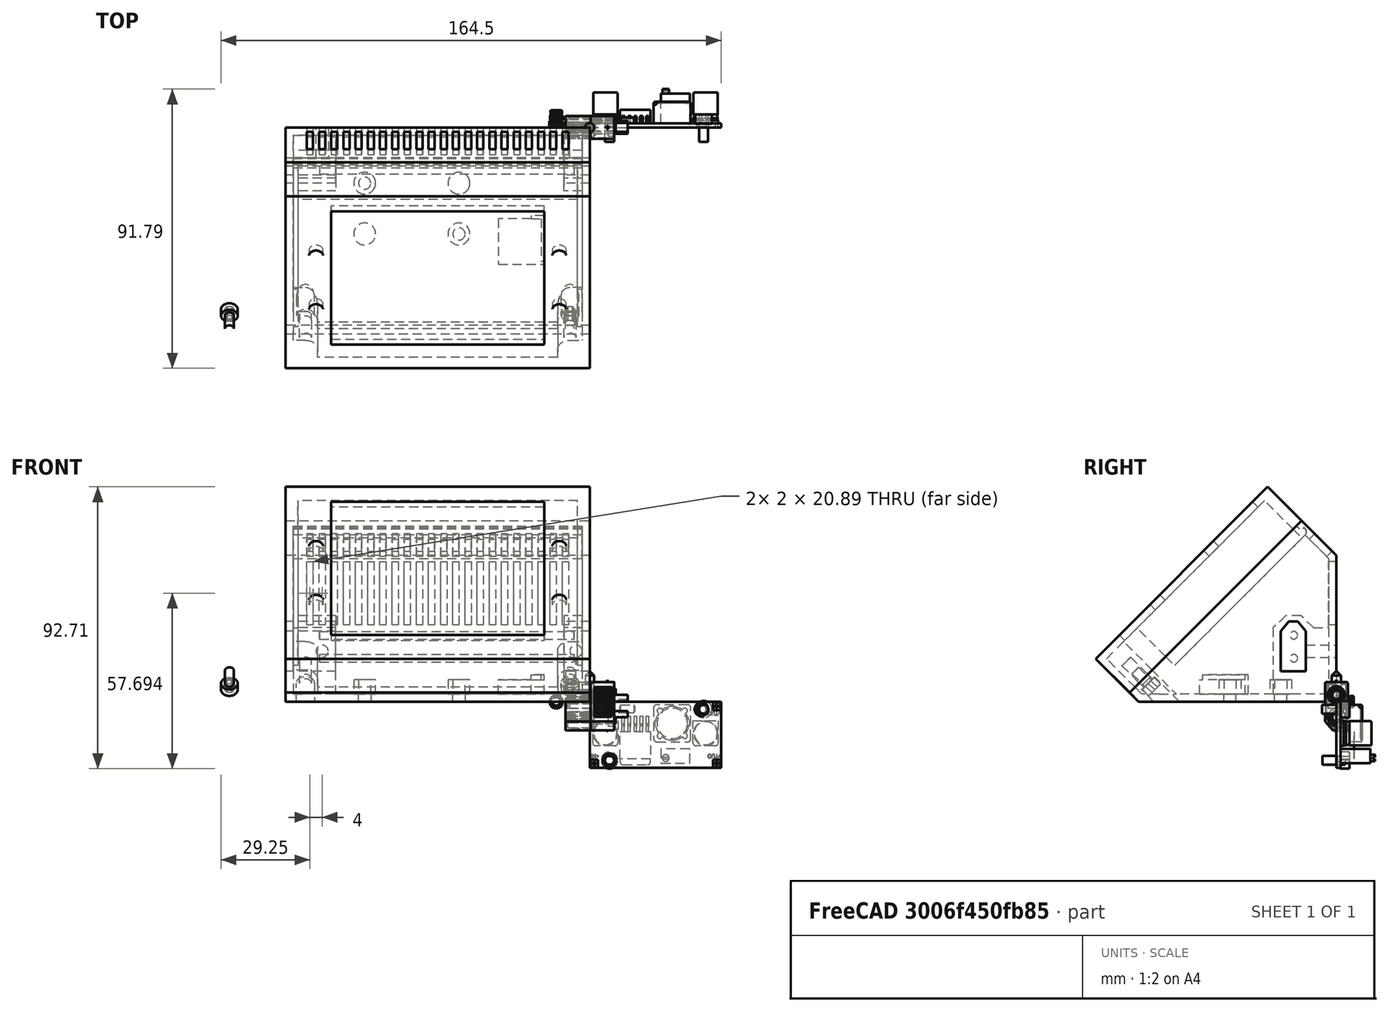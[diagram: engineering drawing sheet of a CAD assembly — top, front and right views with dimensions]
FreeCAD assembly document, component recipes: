
FREECAD ASSEMBLY — COMPONENT RECIPES ("ventilo_014surBase35mm_008.1")

This assembly document has 15 components, labeled P0..P14 below (a component is one placed body or linked part). 9 of them carry a construction recipe — the FreeCAD feature program that regenerates the part from scratch, quoted from this document or its linked companion documents; the rest are supplied as boundary geometry only. No exploded tour is included for this assembly.
COMPONENT P0 — recipe-attached ("base", modeled in this document).
Construction recipe (the document's own serialized feature program — sketch geometry with constraints, then the solid features built on it; lengths are millimeters unless a unit is written):

FEATURE [PartDesign::FeatureBase] Clone
  BaseFeature = -> Slice_child0
FEATURE [PartDesign::Thickness] Thickness
  Base = -> Clone [Face7]
  BaseFeature = -> Clone
  Intersection = false
  Join = 0
  Mode = 0
  Reversed = true
  SupportTransform = false
  Value = 2.5
  expr: Value = <<sp>>.epaisseurParois
FEATURE [PartDesign::Plane] DatumPlane001  label="planXt"
  AttachmentOffset = pos=(0,0,-2.5) rot=(0,0,1;0rad)
  Length = 110.737
  MapMode = 5
  Placement = pos=(-2.5,6e-16,-6e-16) rot=(0.57735,0.57735,0.57735;2.0944rad)
  ResizeMode = 0
  Support = -> [YZ_Plane002]
  Width = 102.305
  expr: .AttachmentOffset.Base.z = -<<sp>>.epaisseurParois
FEATURE [Sketcher::SketchObject] Sketch002  label="sk_renfortXt"
  FullyConstrained = true
  MapMode = 5
  Placement = pos=(-2.5,6e-16,-6e-16) rot=(0.57735,0.57735,0.57735;2.0944rad)
  Support = -> [DatumPlane001]
  expr: .Constraints.dist = <<sp>>.xt60distanceAngleBord
  expr: .Constraints.epRf = <<sp>>.xt60epRenfort
  expr: Constraints[13] = <<sp>>.xt60largeurFetiere
  expr: Constraints[14] = <<sp>>.xt60hauteur
  expr: Constraints[15] = <<sp>>.xt60hauteurToit
  expr: Constraints[16] = <<sp>>.xt60base
  expr: Constraints[18] = .Constraints.dist
  expr: Constraints[31] = <<sp>>.epaisseurParois
  expr: Constraints[32] = .Constraints.epRf
  expr: Constraints[34] = .Constraints.epRf
  expr: Constraints[45] = <<sp>>.epaisseurParois
  sketch-geometry (17):
    g0: LineSegment StartX=-18.3 StartY=10 StartZ=0 EndX=-18.3 EndY=23.25 EndZ=0
    g1: LineSegment StartX=-18.3 StartY=23.25 StartZ=0 EndX=-15.65 EndY=25.75 EndZ=0
    g2: LineSegment StartX=-15.65 StartY=25.75 StartZ=0 EndX=-12.65 EndY=25.75 EndZ=0
    g3: LineSegment StartX=-12.65 StartY=25.75 StartZ=0 EndX=-10 EndY=23.25 EndZ=0
    g4: LineSegment StartX=-10 StartY=23.25 StartZ=0 EndX=-10 EndY=10 EndZ=0
    g5: LineSegment StartX=-10 StartY=10 StartZ=0 EndX=-18.3 EndY=10 EndZ=0
    g6: LineSegment StartX=-14.15 StartY=10 StartZ=0 EndX=-14.15 EndY=25.75 EndZ=0
    g7: LineSegment StartX=-16.6431 StartY=28.25 StartZ=0 EndX=-20.8 EndY=24.3284 EndZ=0
    g8: LineSegment StartX=-20.8 StartY=24.3284 StartZ=0 EndX=-20.8 EndY=2.5 EndZ=0
    g9: LineSegment StartX=-20.8 StartY=2.5 StartZ=0 EndX=-7.5 EndY=2.5 EndZ=0
    g10: LineSegment StartX=-7.5 StartY=2.5 StartZ=0 EndX=-7.5 EndY=24.3284 EndZ=0
    g11: LineSegment StartX=-7.5 StartY=24.3284 StartZ=0 EndX=-11.6569 EndY=28.25 EndZ=0
    g12: LineSegment StartX=-11.6569 StartY=28.25 StartZ=0 EndX=-16.6431 EndY=28.25 EndZ=0
    g13: LineSegment StartX=-7.5 StartY=24.3284 StartZ=0 EndX=-2.5 EndY=24.3284 EndZ=0
    g14: LineSegment StartX=-2.5 StartY=24.3284 StartZ=0 EndX=-2.5 EndY=2.5 EndZ=0
    g15: LineSegment StartX=-2.5 StartY=2.5 StartZ=0 EndX=-7.5 EndY=2.5 EndZ=0
    g16: LineSegment StartX=-7.5 StartY=2.5 StartZ=0 EndX=-7.5 EndY=24.3284 EndZ=0
  constraints (46):
    c: Vertical(g0)
    c: Coincident(g0,g1)
    c: Coincident(g1,g2)
    c: Horizontal(g2)
    c: Coincident(g2,g3)
    c: Coincident(g3,g4)
    c: Vertical(g4)
    c: Coincident(g4,g5)
    c: Coincident(g5,g0)
    c: Horizontal(g5)
    c: Symmetric(g1,g2,g6)
    c: Equal(g0,g4)
    c: Symmetric(g0,g4,g6)
    c: DistanceX(g2,g2) = 3
    c: DistanceY(g4,g4) = 13.25
    c: DistanceY(g3,g2) = 2.5
    c: DistanceX(g5,g5) = 8.3
    c: DistanceX(g4,g-1) = 10  'dist'
    c: DistanceY(g-1,g4) = 10
    c: Coincident(g7,g8)
    c: Vertical(g8)
    c: Coincident(g8,g9)
    c: Horizontal(g9)
    c: Coincident(g9,g10)
    c: Coincident(g10,g11)
    c: Coincident(g11,g12)
    c: Coincident(g12,g7)
    c: Symmetric(g7,g10,g6)
    c: Symmetric(g7,g11,g6)
    c: Symmetric(g8,g9,g6)
    c: DistanceX(g8,g0) = 2.5  'epRf'
    c: DistanceY(g-1,g9) = 2.5
    c: Distance(g7,g1) = 2.5
    c: Parallel(g1,g7)
    c: DistanceY(g2,g11) = 2.5
    c: Coincident(g13,g14)
    c: Coincident(g14,g15)
    c: Coincident(g15,g16)
    c: Coincident(g16,g13)
    c: Horizontal(g13)
    c: Horizontal(g15)
    c: Vertical(g14)
    c: Vertical(g16)
    c: Coincident(g13,g11)
    c: Horizontal(g14,g9)
    c: DistanceX(g14,g-1) = 2.5
FEATURE [PartDesign::Pad] Pad001  label="renfortXt"
  AllowMultiFace = false
  BaseFeature = -> Thickness
  Direction = (1,1,1)
  Length = 95
  Length2 = 100
  Profile = -> Sketch002
  Reversed = true
  Type = 0
  expr: Length = <<sp>>.largeurModuleBase - 2 * <<sp>>.epaisseurParois
FEATURE [Sketcher::SketchObject] Sketch003  label="sk_trouXt"
  FullyConstrained = true
  MapMode = 5
  Placement = pos=(0,0,0) rot=(0.57735,0.57735,0.57735;2.0944rad)
  Support = -> [YZ_Plane002]
  expr: .Constraints.dist = <<sp>>.xt60distanceAngleBord
  expr: Constraints[13] = <<sp>>.xt60base
  expr: Constraints[14] = <<sp>>.xt60hauteur
  expr: Constraints[15] = <<sp>>.xt60hauteurToit + <<sp>>.xtJeu
  expr: Constraints[16] = <<sp>>.xt60largeurFetiere
  expr: Constraints[18] = .Constraints.dist
  sketch-geometry (7):
    g0: LineSegment StartX=-18.3 StartY=10 StartZ=0 EndX=-18.3 EndY=23.25 EndZ=0
    g1: LineSegment StartX=-18.3 StartY=23.25 StartZ=0 EndX=-15.65 EndY=26.35 EndZ=0
    g2: LineSegment StartX=-15.65 StartY=26.35 StartZ=0 EndX=-12.65 EndY=26.35 EndZ=0
    g3: LineSegment StartX=-12.65 StartY=26.35 StartZ=0 EndX=-10 EndY=23.25 EndZ=0
    g4: LineSegment StartX=-10 StartY=23.25 StartZ=0 EndX=-10 EndY=10 EndZ=0
    g5: LineSegment StartX=-10 StartY=10 StartZ=0 EndX=-18.3 EndY=10 EndZ=0
    g6: LineSegment StartX=-14.15 StartY=10 StartZ=0 EndX=-14.15 EndY=26.35 EndZ=0
  constraints (19):
    c: Vertical(g0)
    c: Coincident(g0,g1)
    c: Coincident(g1,g2)
    c: Horizontal(g2)
    c: Coincident(g2,g3)
    c: Coincident(g3,g4)
    c: Coincident(g4,g5)
    c: Coincident(g5,g0)
    c: Horizontal(g5)
    c: Symmetric(g1,g2,g6)
    c: Symmetric(g0,g3,g6)
    c: Vertical(g6)
    c: Symmetric(g0,g4,g6)
    c: DistanceX(g5,g5) = 8.3
    c: DistanceY(g4,g4) = 13.25
    c: DistanceY(g3,g2) = 3.1
    c: DistanceX(g2,g2) = 3
    c: DistanceX(g4,g-1) = 10  'dist'
    c: DistanceY(g-1,g4) = 10
FEATURE [PartDesign::Pocket] Pocket
  AllowMultiFace = false
  BaseFeature = -> Pad001
  Direction = (1,1,1)
  Length = 100
  Length2 = 100
  Profile = -> Sketch003
  Type = 0
  expr: Length = <<sp>>.largeurModuleBase
FEATURE [PartDesign::Plane] DatumPlane002  label="planDecoupeRenfortXt"
  AttachmentOffset = pos=(0,0,2.5) rot=(0,0,1;0rad)
  Length = 145.563
  MapMode = 5
  Placement = pos=(0,-2.5,-6e-16) rot=(1,0,0;1.5708rad)
  ResizeMode = 0
  Support = -> [XZ_Plane002]
  Width = 105.132
  expr: .AttachmentOffset.Base.z = <<sp>>.epaisseurParois
FEATURE [Sketcher::SketchObject] Sketch004  label="sk_decoupRenfXt"
  FullyConstrained = true
  MapMode = 5
  Placement = pos=(0,-2.5,-6e-16) rot=(1,0,0;1.5708rad)
  Support = -> [DatumPlane002]
  expr: Constraints[10] = <<sp>>.xt60LongueurRenfortPetit + <<sp>>.epaisseurParois
  expr: Constraints[11] = <<sp>>.largeurModuleBase - (<<sp>>.xt60longueurRenfortGrand + <<sp>>.epaisseurParois)
  expr: Constraints[8] = <<sp>>.epaisseurParois
  expr: Constraints[9] = <<sp>>.xt60distanceAngleBord + <<sp>>.xt60hauteur + <<sp>>.xt60hauteurToit + <<sp>>.xt60epRenfort
  sketch-geometry (4):
    g0: LineSegment StartX=-83.5 StartY=28.25 StartZ=0 EndX=-8.5 EndY=28.25 EndZ=0
    g1: LineSegment StartX=-8.5 StartY=28.25 StartZ=0 EndX=-8.5 EndY=2.5 EndZ=0
    g2: LineSegment StartX=-8.5 StartY=2.5 StartZ=0 EndX=-83.5 EndY=2.5 EndZ=0
    g3: LineSegment StartX=-83.5 StartY=2.5 StartZ=0 EndX=-83.5 EndY=28.25 EndZ=0
  constraints (12):
    c: Coincident(g0,g1)
    c: Coincident(g1,g2)
    c: Coincident(g2,g3)
    c: Coincident(g3,g0)
    c: Horizontal(g0)
    c: Horizontal(g2)
    c: Vertical(g1)
    c: Vertical(g3)
    c: DistanceY(g-1,g1) = 2.5
    c: DistanceY(g-1,g0) = 28.25
    c: DistanceX(g1,g-1) = 8.5
    c: DistanceX(g2,g-1) = 83.5
FEATURE [PartDesign::Pocket] Pocket001  label="decoupeRenfXt"
  AllowMultiFace = false
  BaseFeature = -> Pocket
  Direction = (1,1,1)
  Length = 23.3
  Length2 = 100
  Profile = -> Sketch004
  Reversed = true
  Type = 0
  expr: Length = <<sp>>.xt60distanceAngleBord + <<sp>>.xt60base + 2 * <<sp>>.xt60epRenfort
FEATURE [Sketcher::SketchObject] Sketch005  label="xt60PercagePostMale"
  FullyConstrained = true
  MapMode = 5
  Placement = pos=(0,0,0) rot=(1,0,0;1.5708rad)
  Support = -> [XZ_Plane002]
  expr: Constraints[0] = <<sp>>.insertDiamPercage
  expr: Constraints[1] = <<sp>>.insertDistanceTrouBordMale
  expr: Constraints[2] = <<sp>>.insertHauteur
  sketch-geometry (1):
    g0: Circle CenterX=-4.5 CenterY=16.625 CenterZ=0 NormalX=0 NormalY=0 NormalZ=1 AngleXU=0 Radius=2
  constraints (3):
    c: Diameter(g0) = 4
    c: DistanceX(g0,g-1) = 4.5
    c: DistanceY(g-1,g0) = 16.625
FEATURE [PartDesign::Pocket] Pocket002  label="insertXtMale"
  AllowMultiFace = false
  BaseFeature = -> Pocket001
  Direction = (1,1,1)
  Length = 10
  Length2 = 100
  Profile = -> Sketch005
  Reversed = true
  Type = 0
  expr: Length = <<sp>>.insertProfondeurPercage
FEATURE [Sketcher::SketchObject] Sketch006  label="xt60PercagePostFem"
  FullyConstrained = true
  MapMode = 5
  Placement = pos=(0,0,0) rot=(1,0,0;1.5708rad)
  Support = -> [XZ_Plane002]
  expr: Constraints[0] = <<sp>>.insertDiamPercage
  expr: Constraints[1] = <<sp>>.insertDistanceTrouBordFem
  expr: Constraints[2] = <<sp>>.insertHauteur
  sketch-geometry (1):
    g0: Circle CenterX=-88 CenterY=16.625 CenterZ=0 NormalX=0 NormalY=0 NormalZ=1 AngleXU=0 Radius=2
  constraints (3):
    c: Diameter(g0) = 4
    c: DistanceX(g0,g-1) = 88
    c: DistanceY(g-1,g0) = 16.625
FEATURE [PartDesign::Pocket] Pocket003  label="insertXt60Fem"
  AllowMultiFace = false
  BaseFeature = -> Pocket002
  Direction = (1,1,1)
  Length = 10
  Length2 = 100
  Profile = -> Sketch006
  Reversed = true
  Type = 0
  expr: Length = <<sp>>.insertProfondeurPercage
FEATURE [PartDesign::Plane] DatumPlane003
  AttachmentOffset = pos=(0,0,2.5) rot=(0,0,1;0rad)
  Length = 146.564
  MapMode = 2
  Placement = pos=(0,0,2.5) rot=(0,0,1;0rad)
  ResizeMode = 0
  Support = -> [XY_Plane002]
  Width = 114.564
  expr: .AttachmentOffset.Base.z = <<sp>>.epaisseurParois
FEATURE [PartDesign::Plane] DatumPlane004  label="planTrancheur"
  AttachmentOffset = pos=(0,0,71) rot=(-1,0,0;0.785398rad)
  Length = 150.056
  MapMode = 5
  Placement = pos=(0,-71,-1.58e-14) rot=(1,0,0;0.785398rad)
  ResizeMode = 0
  Support = -> [XZ_Plane002]
  Width = 150.616
  expr: .AttachmentOffset.Base.z = <<sp>>.planTrancheur
FEATURE [Sketcher::SketchObject] Sketch008
  FullyConstrained = true
  MapMode = 5
  Placement = pos=(0,-71,-2.13e-14) rot=(1,0,0;0.785398rad)
  Support = -> [DatumPlane004]
  expr: .Constraints.dist = <<sp>>.epaisseurParois
  expr: Constraints[13] = <<sp>>.epaisseurParois
  expr: Constraints[16] = <<sp>>.insertDiamPercage / 2 + <<sp>>.insertFAVMargeDist
  expr: Constraints[1] = <<sp>>.insertFavDistAuZeroDuPLan
  expr: Constraints[21] = <<sp>>.insertFAVDistBord
  expr: Constraints[22] = <<sp>>.largeurModuleBase - <<sp>>.epaisseurParois
  sketch-geometry (7):
    g0: LineSegment StartX=-2.5 StartY=4.24264 StartZ=0 EndX=-97.5 EndY=4.24264 EndZ=0
    g1: LineSegment StartX=-6.5 StartY=14.7426 StartZ=0 EndX=-2.5 EndY=14.7426 EndZ=0
    g2: LineSegment StartX=-2.5 StartY=14.7426 StartZ=0 EndX=-2.5 EndY=6.74264 EndZ=0
    g3: LineSegment StartX=-2.5 StartY=6.74264 StartZ=0 EndX=-10.5 EndY=6.74264 EndZ=0
    g4: LineSegment StartX=-10.5 StartY=6.74264 StartZ=0 EndX=-10.5 EndY=10.7426 EndZ=0
    g5: ArcOfCircle CenterX=-6.5 CenterY=10.7426 CenterZ=0 NormalX=0 NormalY=0 NormalZ=1 AngleXU=0 Radius=4 StartAngle=1.5708 EndAngle=3.14159
    g6: LineSegment StartX=-6.5 StartY=10.7426 StartZ=0 EndX=-6.5 EndY=6.74264 EndZ=0
  constraints (23):
    c: Horizontal(g0)
    c: DistanceY(g-1,g0) = 4.24264
    c: DistanceX(g0,g-1) = 2.5  'dist'
    c: Horizontal(g1)
    c: Coincident(g1,g2)
    c: Vertical(g2)
    c: Coincident(g2,g3)
    c: Horizontal(g3)
    c: Coincident(g3,g4)
    c: Vertical(g4)
    c: Vertical(g2,g0)
    c: Equal(g3,g2)
    c: Equal(g4,g1)
    c: DistanceY(g0,g2) = 2.5
    c: Coincident(g5,g4)
    c: Coincident(g5,g1)
    c: DistanceX(g5,g2) = 4
    c: Coincident(g6,g5)
    c: PointOnObject(g6,g3)
    c: Vertical(g6)
    c: Vertical(g5,g1)
    c: DistanceX(g3,g3) = 8
    c: DistanceX(g0,g-1) = 97.5
FEATURE [PartDesign::Pad] Pad003  label="padTrouFAVDroite"
  AllowMultiFace = false
  BaseFeature = -> Pocket003
  Direction = (1,1,1)
  Length = 10
  Length2 = 100
  Profile = -> Sketch008
  Reversed = true
  Type = 3
  UpToFace = -> DatumPlane003
FEATURE [Sketcher::SketchObject] Sketch009
  FullyConstrained = true
  MapMode = 5
  Placement = pos=(0,-71,-2.13e-14) rot=(1,0,0;0.785398rad)
  Support = -> [DatumPlane004]
  expr: .Constraints.larg = <<sp>>.insertFAVDistBord
  expr: Constraints[11] = .Constraints.larg / 2
  expr: Constraints[12] = <<sp>>.largeurModuleBase
  expr: Constraints[13] = <<sp>>.insertFavDistAuZeroDuPLan
  expr: Constraints[14] = <<sp>>.epaisseurParois
  expr: Constraints[15] = <<sp>>.epaisseurParois
  expr: Constraints[8] = .Constraints.larg
  sketch-geometry (6):
    g0: LineSegment StartX=-97.5 StartY=6.74264 StartZ=0 EndX=-89.5 EndY=6.74264 EndZ=0
    g1: LineSegment StartX=-89.5 StartY=6.74264 StartZ=0 EndX=-89.5 EndY=10.7426 EndZ=0
    g2: LineSegment StartX=-93.5 StartY=14.7426 StartZ=0 EndX=-97.5 EndY=14.7426 EndZ=0
    g3: LineSegment StartX=-97.5 StartY=14.7426 StartZ=0 EndX=-97.5 EndY=6.74264 EndZ=0
    g4: ArcOfCircle CenterX=-93.5 CenterY=10.7426 CenterZ=0 NormalX=0 NormalY=0 NormalZ=1 AngleXU=0 Radius=4 StartAngle=1e-16 EndAngle=1.5708
    g5: GeomPoint X=-100 Y=4.24264 Z=0
  constraints (16):
    c: Coincident(g0,g1)
    c: Coincident(g2,g3)
    c: Coincident(g3,g0)
    c: Horizontal(g0)
    c: Horizontal(g2)
    c: Vertical(g1)
    c: Vertical(g3)
    c: DistanceX(g0,g0) = 8  'larg'
    c: DistanceY(g3,g3) = 8
    c: Tangent(g2,g4) = -1.5708
    c: Tangent(g1,g4) = -1.5708
    c: DistanceX(g0,g4) = 4
    c: DistanceX(g5,g-1) = 100
    c: DistanceY(g-1,g5) = 4.24264
    c: DistanceX(g5,g0) = 2.5
    c: DistanceY(g5,g0) = 2.5
FEATURE [PartDesign::Pad] Pad004  label="padTrouFavGauche"
  AllowMultiFace = false
  BaseFeature = -> Pad003
  Direction = (1,1,1)
  Length = 10
  Length2 = 100
  Profile = -> Sketch009
  Type = 3
  UpToFace = -> DatumPlane003 [Plane]
FEATURE [Sketcher::SketchObject] Sketch010
  FullyConstrained = true
  MapMode = 5
  Placement = pos=(0,-71,-2.13e-14) rot=(1,0,0;0.785398rad)
  Support = -> [DatumPlane004]
  expr: Constraints[0] = <<sp>>.insertFAVDistBord / 2 + <<sp>>.epaisseurParois
  expr: Constraints[1] = <<sp>>.insertFavDistAuZeroDuPLan + <<sp>>.epaisseurParois + <<sp>>.insertFAVDistBord / 2
  expr: Constraints[2] = <<sp>>.insertDiamPercage
  sketch-geometry (1):
    g0: Circle CenterX=-6.5 CenterY=10.7426 CenterZ=0 NormalX=0 NormalY=0 NormalZ=1 AngleXU=0 Radius=2
  constraints (3):
    c: DistanceX(g0,g-1) = 6.5
    c: DistanceY(g-1,g0) = 10.7426
    c: Diameter(g0) = 4
FEATURE [PartDesign::Pocket] Pocket004  label="trouDroit"
  AllowMultiFace = false
  BaseFeature = -> Pad004
  Direction = (1,1,1)
  Length = 5
  Length2 = 100
  Profile = -> Sketch010
  Type = 1
FEATURE [Sketcher::SketchObject] Sketch011
  FullyConstrained = true
  MapMode = 5
  Placement = pos=(0,-71,-2.13e-14) rot=(1,0,0;0.785398rad)
  Support = -> [DatumPlane004]
  expr: Constraints[0] = <<sp>>.insertDiamPercage
  expr: Constraints[1] = <<sp>>.largeurModuleBase - <<sp>>.epaisseurParois - <<sp>>.insertFAVDistBord / 2
  expr: Constraints[2] = <<sp>>.insertFavDistAuZeroDuPLan + <<sp>>.epaisseurParois + <<sp>>.insertFAVDistBord / 2
  sketch-geometry (1):
    g0: Circle CenterX=-93.5 CenterY=10.7426 CenterZ=0 NormalX=0 NormalY=0 NormalZ=1 AngleXU=0 Radius=2
  constraints (3):
    c: Diameter(g0) = 4
    c: DistanceX(g0,g-1) = 93.5
    c: DistanceY(g-1,g0) = 10.7426
FEATURE [PartDesign::Pocket] Pocket005  label="trouGauche"
  AllowMultiFace = false
  BaseFeature = -> Pocket004
  Direction = (1,1,1)
  Length = 5
  Length2 = 100
  Profile = -> Sketch011
  Type = 1
FEATURE [PartDesign::Plane] DatumPlane005  label="planTeteVisFav"
  AttachmentOffset = pos=(0,0,68) rot=(-1,0,0;0.785398rad)
  Length = 150.056
  MapMode = 5
  Placement = pos=(0,-68,-1.51e-14) rot=(1,0,0;0.785398rad)
  ResizeMode = 0
  Support = -> [XZ_Plane002]
  Width = 150.616
  expr: .AttachmentOffset.Base.z = <<sp>>.planTrancheur - 3
FEATURE [Sketcher::SketchObject] Sketch012
  ExternalGeometry = -> [Pocket005]
  FullyConstrained = true
  MapMode = 5
  Placement = pos=(0,-68,-1.42e-14) rot=(1,0,0;0.785398rad)
  Support = -> [DatumPlane005]
  expr: Constraints[1] = <<sp>>.visM3DiamEncastrement
  sketch-geometry (2):
    g0: Circle CenterX=-6.5 CenterY=8.62132 CenterZ=0 NormalX=0 NormalY=0 NormalZ=1 AngleXU=0 Radius=3
    g1: Circle CenterX=-93.5 CenterY=8.62132 CenterZ=0 NormalX=0 NormalY=0 NormalZ=1 AngleXU=0 Radius=3
  constraints (4):
    c: Equal(g0,g1)
    c: Diameter(g1) = 6
    c: Coincident(g1,g-4)
    c: Coincident(g-3,g0)
FEATURE [PartDesign::Pocket] Pocket006  label="evidementTeteVisFav"
  AllowMultiFace = false
  BaseFeature = -> Pocket005
  Direction = (1,1,1)
  Length = 20
  Length2 = 100
  Profile = -> Sketch012
  Type = 1
FEATURE [Sketcher::SketchObject] Sketch014
  FullyConstrained = true
  MapMode = 5
  Placement = pos=(0,0,0) rot=(1,0,0;1.5708rad)
  Support = -> [XZ_Plane002]
  expr: Constraints[12] = <<sp>>.xt60distanceAngleBord + <<sp>>.xt60hauteur + <<sp>>.ventilDistBordFente
  expr: Constraints[13] = <<sp>>.ventilLargeurFentes
  expr: Constraints[14] = <<sp>>.ventilEcartfente / 2
  expr: Constraints[15] = <<sp>>.hauteurDuDos - <<sp>>.ventilDistBordFente
  expr: Constraints[2] = <<sp>>.hauteurDuDos
  expr: Constraints[3] = <<sp>>.largeurModuleBase / 2
  sketch-geometry (5):
    g0: LineSegment StartX=-50 StartY=0 StartZ=0 EndX=-50 EndY=48.1371 EndZ=0
    g1: LineSegment StartX=-53 StartY=46.1371 StartZ=0 EndX=-51 EndY=46.1371 EndZ=0
    g2: LineSegment StartX=-51 StartY=46.1371 StartZ=0 EndX=-51 EndY=25.25 EndZ=0
    g3: LineSegment StartX=-51 StartY=25.25 StartZ=0 EndX=-53 EndY=25.25 EndZ=0
    g4: LineSegment StartX=-53 StartY=25.25 StartZ=0 EndX=-53 EndY=46.1371 EndZ=0
  constraints (16):
    c: PointOnObject(g0,g-1)
    c: Vertical(g0)
    c: DistanceY(g0,g0) = 48.1371
    c: DistanceX(g0,g-1) = 50
    c: Coincident(g1,g2)
    c: Coincident(g2,g3)
    c: Coincident(g3,g4)
    c: Coincident(g4,g1)
    c: Horizontal(g1)
    c: Horizontal(g3)
    c: Vertical(g2)
    c: Vertical(g4)
    c: DistanceY(g-1,g2) = 25.25
    c: DistanceX(g1,g1) = 2
    c: DistanceX(g2,g0) = 1
    c: DistanceY(g-1,g1) = 46.1371
FEATURE [PartDesign::Pocket] Pocket008  label="ventilFente1"
  AllowMultiFace = false
  BaseFeature = -> Pocket006
  Direction = (1,1,1)
  Length = 2.5
  Length2 = 100
  Profile = -> Sketch014
  Reversed = true
  Type = 0
  expr: Length = <<sp>>.epaisseurParois
FEATURE [PartDesign::LinearPattern] LinearPattern  label="ventilDosRepeat1"
  BaseFeature = -> Pocket008
  Direction = -> Sketch014 [H_Axis]
  Length = 40
  Occurrences = 11
  Originals = -> [Pocket008]
  Reversed = true
  expr: Length = <<sp>>.ventilLargeurRepet
  expr: Occurrences = <<sp>>.ventilNbrFents
FEATURE [PartDesign::LinearPattern] LinearPattern001  label="ventilDosRepeat2"
  BaseFeature = -> LinearPattern
  Direction = -> Sketch014 [H_Axis]
  Length = 44
  Occurrences = 12
  Originals = -> [Pocket008]
  expr: Length = <<sp>>.ventilLargeurRepet + <<sp>>.ventilEcartfente + <<sp>>.ventilLargeurFentes
  expr: Occurrences = <<sp>>.ventilNbrFents + 1
FEATURE [PartDesign::Plane] DatumPlane006  label="planVentilSup"
  AttachmentOffset = pos=(0,0,-48.1371) rot=(1,0,0;0.785398rad)
  Length = 150.056
  MapMode = 5
  Placement = pos=(0,48.1371,1.07e-14) rot=(1,0,0;2.35619rad)
  ResizeMode = 0
  Support = -> [XZ_Plane002]
  Width = 150.616
  expr: .AttachmentOffset.Base.z = -<<sp>>.hauteurDuDos
FEATURE [Sketcher::SketchObject] Sketch015
  FullyConstrained = true
  MapMode = 5
  Placement = pos=(0,48.1371,1.07e-14) rot=(1,0,0;2.35619rad)
  Support = -> [DatumPlane006]
  expr: Constraints[10] = <<sp>>.ventilLargeurFentes
  expr: Constraints[11] = (<<sp>>.largeurModuleBase + <<sp>>.ventilEcartfente) / 2
  expr: Constraints[8] = <<sp>>.distanceAuZeroPlanBorArriere + <<sp>>.ventilDistBordFente
  expr: Constraints[9] = <<sp>>.longPetitRetSupSansFav - 2 * <<sp>>.ventilDistBordFente - <<sp>>.favBordureProf
  sketch-geometry (4):
    g0: LineSegment StartX=-51 StartY=78.0926 StartZ=0 EndX=-53 EndY=78.0926 EndZ=0
    g1: LineSegment StartX=-53 StartY=78.0926 StartZ=0 EndX=-53 EndY=70.0761 EndZ=0
    g2: LineSegment StartX=-53 StartY=70.0761 StartZ=0 EndX=-51 EndY=70.0761 EndZ=0
    g3: LineSegment StartX=-51 StartY=70.0761 StartZ=0 EndX=-51 EndY=78.0926 EndZ=0
  constraints (12):
    c: Coincident(g0,g1)
    c: Coincident(g1,g2)
    c: Coincident(g2,g3)
    c: Coincident(g3,g0)
    c: Horizontal(g0)
    c: Horizontal(g2)
    c: Vertical(g1)
    c: Vertical(g3)
    c: DistanceY(g-1,g2) = 70.0761
    c: DistanceY(g2,g0) = 8.01652
    c: DistanceX(g0,g0) = 2
    c: DistanceX(g2,g-1) = 51
FEATURE [PartDesign::Pocket] Pocket009  label="ventilSupFente"
  AllowMultiFace = false
  BaseFeature = -> LinearPattern001
  Direction = (1,1,1)
  Length = 5
  Length2 = 100
  Profile = -> Sketch015
  Reversed = true
  Type = 0
FEATURE [PartDesign::LinearPattern] LinearPattern002  label="ventilSupRepeat1"
  BaseFeature = -> Pocket009
  Direction = -> Sketch015 [H_Axis]
  Length = 40
  Occurrences = 11
  Originals = -> [Pocket009]
  Reversed = true
  expr: Length = <<sp>>.ventilLargeurRepet
  expr: Occurrences = <<sp>>.ventilNbrFents
FEATURE [PartDesign::LinearPattern] LinearPattern003  label="ventilSupRepeat2"
  BaseFeature = -> LinearPattern002
  Direction = -> Sketch015 [H_Axis]
  Length = 44
  Occurrences = 12
  Originals = -> [Pocket009]
  expr: Length = <<sp>>.ventilLargeurRepet + <<sp>>.ventilEcartfente + <<sp>>.ventilLargeurFentes
  expr: Occurrences = <<sp>>.ventilNbrFents + 1
FEATURE [PartDesign::Body] Body001  label="base"
  BaseFeature = -> Slice_child0
  Group = -> [Clone,Thickness,DatumPlane001,Sketch002,Pad001,Sketch003,Pocket,DatumPlane002,Sketch004,Pocket001,Sketch005,Pocket002,Sketch006,Pocket003,DatumPlane003,DatumPlane004,Sketch008,Pad003,Sketch009,Pad004,Sketch010,Pocket004,Sketch011,Pocket005,DatumPlane005,Sketch012,Pocket006,Sketch014,Pocket008,LinearPattern,LinearPattern001,DatumPlane006,Sketch015,Pocket009,LinearPattern002,LinearPattern003,+11 more]
  Origin = -> Origin002
  Tip = -> Pad028
COMPONENT P1 — recipe-attached ("faceAvant", modeled in this document).
Construction recipe (the document's own serialized feature program — sketch geometry with constraints, then the solid features built on it; lengths are millimeters unless a unit is written):

FEATURE [PartDesign::FeatureBase] Clone001
  BaseFeature = -> Slice_child1
FEATURE [PartDesign::Thickness] Thickness001
  Base = -> Clone001 [Face5]
  BaseFeature = -> Clone001
  Intersection = false
  Join = 0
  Mode = 0
  Reversed = true
  SupportTransform = false
  Value = 2.5
  expr: Value = <<sp>>.epaisseurParois
FEATURE [PartDesign::Plane] DatumPlane007  label="planTrancheurBis"
  AttachmentOffset = pos=(0,0,71) rot=(-1,0,0;0.785398rad)
  Length = 151.582
  MapMode = 5
  Placement = pos=(0,-71,-1.58e-14) rot=(1,0,0;0.785398rad)
  ResizeMode = 0
  Support = -> [XZ_Plane003]
  Width = 167.899
  expr: .AttachmentOffset.Base.z = <<sp>>.planTrancheur
FEATURE [Sketcher::SketchObject] Sketch016  label="sk_insertFavDroit"
  FullyConstrained = true
  MapMode = 5
  Placement = pos=(0,-71,-2.13e-14) rot=(1,0,0;0.785398rad)
  Support = -> [DatumPlane007]
  expr: Constraints[11] = <<sp>>.insertFAVDistBord
  expr: Constraints[14] = <<sp>>.insertFAVDistBord / 2
  expr: Constraints[7] = <<sp>>.epaisseurParois
  expr: Constraints[8] = <<sp>>.insertFavDistAuZeroDuPLan + <<sp>>.epaisseurParois
  expr: Constraints[9] = <<sp>>.insertFAVDistBord
  sketch-geometry (5):
    g0: LineSegment StartX=-6.5 StartY=14.7426 StartZ=0 EndX=-2.5 EndY=14.7426 EndZ=0
    g1: LineSegment StartX=-2.5 StartY=14.7426 StartZ=0 EndX=-2.5 EndY=6.74264 EndZ=0
    g2: LineSegment StartX=-2.5 StartY=6.74264 StartZ=0 EndX=-10.5 EndY=6.74264 EndZ=0
    g3: LineSegment StartX=-10.5 StartY=6.74264 StartZ=0 EndX=-10.5 EndY=10.7426 EndZ=0
    g4: ArcOfCircle CenterX=-6.5 CenterY=10.7426 CenterZ=0 NormalX=0 NormalY=0 NormalZ=1 AngleXU=0 Radius=4 StartAngle=1.5708 EndAngle=3.14159
  constraints (15):
    c: Horizontal(g0)
    c: Coincident(g0,g1)
    c: Vertical(g1)
    c: Coincident(g1,g2)
    c: Horizontal(g2)
    c: Coincident(g2,g3)
    c: Vertical(g3)
    c: DistanceX(g1,g-1) = 2.5
    c: DistanceY(g-1,g1) = 6.74264
    c: DistanceY(g1,g1) = 8
    c: Equal(g3,g0)
    c: DistanceX(g2,g2) = 8
    c: Coincident(g4,g0)
    c: Tangent(g4,g3) = 1.5708
    c: DistanceX(g4,g1) = 4
FEATURE [PartDesign::Pad] Pad005  label="padInsertFavDroit"
  AllowMultiFace = false
  BaseFeature = -> Thickness001
  Direction = (1,1,1)
  Length = 10
  Length2 = 100
  Profile = -> Sketch016
  Type = 2
FEATURE [Sketcher::SketchObject] Sketch017  label="sp_padInserFavGauch"
  FullyConstrained = true
  MapMode = 5
  Placement = pos=(0,-71,-2.13e-14) rot=(1,0,0;0.785398rad)
  Support = -> [DatumPlane007]
  expr: Constraints[10] = <<sp>>.insertFAVDistBord
  expr: Constraints[12] = <<sp>>.insertFAVDistBord / 2
  expr: Constraints[13] = <<sp>>.largeurModuleBase
  expr: Constraints[14] = <<sp>>.insertFavDistAuZeroDuPLan
  expr: Constraints[15] = <<sp>>.epaisseurParois
  expr: Constraints[16] = <<sp>>.epaisseurParois
  sketch-geometry (6):
    g0: LineSegment StartX=-93.5 StartY=14.7426 StartZ=0 EndX=-97.5 EndY=14.7426 EndZ=0
    g1: LineSegment StartX=-97.5 StartY=14.7426 StartZ=0 EndX=-97.5 EndY=6.74264 EndZ=0
    g2: LineSegment StartX=-97.5 StartY=6.74264 StartZ=0 EndX=-89.5 EndY=6.74264 EndZ=0
    g3: LineSegment StartX=-89.5 StartY=6.74264 StartZ=0 EndX=-89.5 EndY=10.7426 EndZ=0
    g4: ArcOfCircle CenterX=-93.5 CenterY=10.7426 CenterZ=0 NormalX=0 NormalY=0 NormalZ=1 AngleXU=0 Radius=4 StartAngle=0 EndAngle=1.5708
    g5: GeomPoint X=-100 Y=4.24264 Z=0
  constraints (17):
    c: Horizontal(g0)
    c: Coincident(g0,g1)
    c: Vertical(g1)
    c: Coincident(g1,g2)
    c: Horizontal(g2)
    c: Coincident(g2,g3)
    c: Vertical(g3)
    c: Equal(g3,g0)
    c: Equal(g2,g1)
    c: Coincident(g0,g4)
    c: DistanceX(g2,g2) = 8
    c: Tangent(g4,g3) = -1.5708
    c: DistanceX(g0,g0) = 4
    c: DistanceX(g5,g-1) = 100
    c: DistanceY(g-1,g5) = 4.24264
    c: DistanceY(g5,g1) = 2.5
    c: DistanceX(g5,g1) = 2.5
FEATURE [PartDesign::Pad] Pad006  label="padInsertFavGauch"
  AllowMultiFace = false
  BaseFeature = -> Pad005
  Direction = (1,1,1)
  Length = 10
  Length2 = 100
  Profile = -> Sketch017
  Type = 2
FEATURE [Sketcher::SketchObject] Sketch018  label="skPercageInsertFavDroit"
  FullyConstrained = true
  MapMode = 5
  Placement = pos=(0,-71,-2.13e-14) rot=(1,0,0;0.785398rad)
  Support = -> [DatumPlane007]
  expr: Constraints[0] = <<sp>>.insertDiamPercage
  expr: Constraints[1] = <<sp>>.insertFavDistAuZeroDuPLan + <<sp>>.epaisseurParois + <<sp>>.insertFAVDistBord / 2
  expr: Constraints[2] = <<sp>>.epaisseurParois + <<sp>>.insertFAVDistBord / 2
  expr: Constraints[7] = <<sp>>.largeurModuleBase - 2 * <<sp>>.epaisseurParois - <<sp>>.insertFAVDistBord
  sketch-geometry (3):
    g0: Circle CenterX=-6.5 CenterY=10.7426 CenterZ=0 NormalX=0 NormalY=0 NormalZ=1 AngleXU=0 Radius=2
    g1: Circle CenterX=-93.5 CenterY=10.7426 CenterZ=0 NormalX=0 NormalY=0 NormalZ=1 AngleXU=0 Radius=2
    g2: LineSegment StartX=-93.5 StartY=10.7426 StartZ=0 EndX=-6.5 EndY=10.7426 EndZ=0
  constraints (8):
    c: Diameter(g0) = 4
    c: DistanceY(g-1,g0) = 10.7426
    c: DistanceX(g0,g-1) = 6.5
    c: Equal(g0,g1)
    c: Coincident(g2,g1)
    c: Coincident(g2,g0)
    c: Horizontal(g2)
    c: DistanceX(g2,g2) = 87
FEATURE [PartDesign::Pocket] Pocket010  label="trouInsertFavDroit"
  AllowMultiFace = false
  BaseFeature = -> Pad006
  Direction = (1,1,1)
  Length = 8
  Length2 = 100
  Profile = -> Sketch018
  Reversed = true
  Type = 0
  expr: Length = <<sp>>.insertFavProfondeur
FEATURE [PartDesign::Plane] DatumPlane011  label="planFaceAvant"
  AttachmentOffset = pos=(0,0,93.2843) rot=(-1,0,0;0.785398rad)
  Length = 151.582
  MapMode = 5
  Placement = pos=(0,-93.2843,-2.07e-14) rot=(1,0,0;0.785398rad)
  ResizeMode = 0
  Support = -> [XZ_Plane003]
  Width = 167.899
  expr: .AttachmentOffset.Base.z = <<sp>>.planFaceAvant
FEATURE [Sketcher::SketchObject] Sketch030  label="sk_rebordFav"
  FullyConstrained = true
  MapMode = 5
  Placement = pos=(0,-71,-2.13e-14) rot=(1,0,0;0.785398rad)
  Support = -> [DatumPlane007]
  expr: Constraints[0] = <<sp>>.insertFavDistAuZeroDuPLan
  expr: Constraints[19] = <<sp>>.epaisseurParois
  expr: Constraints[20] = <<sp>>.favEpBordure
  expr: Constraints[21] = <<sp>>.favDistBordPlan
  expr: Constraints[22] = <<sp>>.largeurModuleBase - 2 * <<sp>>.epaisseurParois
  expr: Constraints[23] = <<sp>>.favEpBordure
  expr: Constraints[24] = <<sp>>.Face - <<sp>>.epaisseurParois
  expr: Constraints[25] = <<sp>>.favEpBordure
  sketch-geometry (9):
    g0: GeomPoint X=0 Y=4.24264 Z=0
    g1: LineSegment StartX=-97.5 StartY=20.9853 StartZ=0 EndX=-97.5 EndY=81.7426 EndZ=0
    g2: LineSegment StartX=-97.5 StartY=81.7426 StartZ=0 EndX=-2.5 EndY=81.7426 EndZ=0
    g3: LineSegment StartX=-2.5 StartY=81.7426 StartZ=0 EndX=-2.5 EndY=20.9853 EndZ=0
    g4: LineSegment StartX=-2.5 StartY=20.9853 StartZ=0 EndX=-4 EndY=20.9853 EndZ=0
    g5: LineSegment StartX=-4 StartY=20.9853 StartZ=0 EndX=-4 EndY=80.2426 EndZ=0
    g6: LineSegment StartX=-4 StartY=80.2426 StartZ=0 EndX=-96 EndY=80.2426 EndZ=0
    g7: LineSegment StartX=-96 StartY=80.2426 StartZ=0 EndX=-96 EndY=20.9853 EndZ=0
    g8: LineSegment StartX=-96 StartY=20.9853 StartZ=0 EndX=-97.5 EndY=20.9853 EndZ=0
  constraints (26):
    c: DistanceY(g-1,g0) = 4.24264
    c: Vertical(g0,g-1)
    c: Vertical(g1)
    c: Coincident(g1,g2)
    c: Horizontal(g2)
    c: Coincident(g2,g3)
    c: Vertical(g3)
    c: Coincident(g3,g4)
    c: Horizontal(g4)
    c: Coincident(g4,g5)
    c: Vertical(g5)
    c: Coincident(g5,g6)
    c: Horizontal(g6)
    c: Coincident(g6,g7)
    c: Vertical(g7)
    c: Coincident(g7,g8)
    c: Coincident(g8,g1)
    c: Horizontal(g8)
    c: Horizontal(g7,g4)
    c: DistanceX(g3,g0) = 2.5
    c: DistanceX(g4,g4) = 1.5
    c: DistanceY(g0,g3) = 16.7426
    c: DistanceX(g1,g3) = 95
    c: DistanceY(g5,g2) = 1.5
    c: DistanceY(g0,g2) = 77.5
    c: DistanceX(g1,g7) = 1.5
FEATURE [PartDesign::Pad] Pad014  label="favRebordSupport"
  AllowMultiFace = false
  BaseFeature = -> Pocket010
  Direction = (1,1,1)
  Length = 10
  Length2 = 100
  Profile = -> Sketch030
  Type = 3
  UpToFace = -> Pocket010 [Face13]
FEATURE [PartDesign::Pad] Pad015  label="favRebord"
  AllowMultiFace = false
  BaseFeature = -> Pad014
  Direction = (1,1,1)
  Length = 4.15
  Length2 = 100
  Profile = -> Sketch030
  Reversed = true
  Type = 0
  expr: Length = <<sp>>.favBordureProf
FEATURE [Sketcher::SketchObject] Sketch031  label="sk_bourlet"
  ExternalGeometry = -> [Pad015]
  FullyConstrained = true
  MapMode = 5
  Placement = pos=(-2.5,0,0) rot=(0.57735,0.57735,0.57735;2.0944rad)
  Support = -> [Pad015]
  expr: Constraints[3] = <<sp>>.bourletMaintientRayon - <<sp>>.bourletRayonJeu
  sketch-geometry (2):
    g0: ArcOfCircle CenterX=-11.184 CenterY=55.7855 CenterZ=0 NormalX=0 NormalY=0 NormalZ=1 AngleXU=0 Radius=1.3 StartAngle=5.49779 EndAngle=8.63938
    g1: LineSegment StartX=-12.1032 StartY=56.7048 StartZ=0 EndX=-10.2647 EndY=54.8663 EndZ=0
  constraints (6):
    c: Coincident(g0,g-3)
    c: PointOnObject(g0,g-3)
    c: PointOnObject(g0,g-3)
    c: Radius(g0) = 1.3
    c: Coincident(g1,g0)
    c: Coincident(g1,g0)
FEATURE [PartDesign::Pad] Pad016  label="bourlet"
  AllowMultiFace = false
  BaseFeature = -> Pad015
  Direction = (1,1,1)
  Length = 10
  Length2 = 100
  Profile = -> Sketch031
  Reversed = true
  Type = 3
  UpToFace = -> Pad015 [Face11]
FEATURE [Sketcher::SketchObject] Sketch051
  FullyConstrained = true
  MapMode = 5
  Placement = pos=(0,-93.2843,-2.84e-14) rot=(1,0,0;0.785398rad)
  Support = -> [DatumPlane011]
  expr: Constraints[21] = <<favSp>>.fanSubSystemTrouDiam + <<favSp>>.favJeu
  expr: Constraints[22] = <<favSp>>.fanSubSystemEntraxX
  expr: Constraints[23] = <<favSp>>.fanSubSystemEntraxY
  expr: Constraints[24] = <<favSp>>.fanSubSystemCavitLong
  expr: Constraints[25] = <<favSp>>.fanSubSystemCaviteLarg
  expr: Constraints[26] = <<favSp>>.fanSubSystemPosY
  expr: Constraints[31] = <<favSp>>.fanSubSystemEntraxeCenterPosY
  expr: Constraints[9] = <<favSp>>.fanSubSystemPosX
  sketch-geometry (13):
    g0: LineSegment StartX=-85 StartY=93 StartZ=0 EndX=-15 EndY=93 EndZ=0
    g1: LineSegment StartX=-15 StartY=93 StartZ=0 EndX=-15 EndY=31 EndZ=0
    g2: LineSegment StartX=-15 StartY=31 StartZ=0 EndX=-85 EndY=31 EndZ=0
    g3: LineSegment StartX=-85 StartY=31 StartZ=0 EndX=-85 EndY=93 EndZ=0
    g4: Circle CenterX=-90 CenterY=72.5 CenterZ=0 NormalX=0 NormalY=0 NormalZ=1 AngleXU=0 Radius=2.25
    g5: Circle CenterX=-10 CenterY=72.5 CenterZ=0 NormalX=0 NormalY=0 NormalZ=1 AngleXU=0 Radius=2.25
    g6: Circle CenterX=-10 CenterY=47.5 CenterZ=0 NormalX=0 NormalY=0 NormalZ=1 AngleXU=0 Radius=2.25
    g7: Circle CenterX=-90 CenterY=47.5 CenterZ=0 NormalX=0 NormalY=0 NormalZ=1 AngleXU=0 Radius=2.25
    g8: GeomPoint X=-50 Y=31 Z=0
    g9: LineSegment StartX=-50 StartY=31 StartZ=0 EndX=-50 EndY=93 EndZ=0
    g10: LineSegment StartX=-85 StartY=62 StartZ=0 EndX=-15 EndY=62 EndZ=0
    g11: LineSegment StartX=-10 StartY=47.5 StartZ=0 EndX=-10 EndY=72.5 EndZ=0
    g12: GeomPoint X=-10 Y=60 Z=0
  constraints (32):
    c: Coincident(g0,g1)
    c: Coincident(g1,g2)
    c: Coincident(g2,g3)
    c: Coincident(g3,g0)
    c: Horizontal(g0)
    c: Horizontal(g2)
    c: Vertical(g1)
    c: Vertical(g3)
    c: Symmetric(g2,g1,g8)
    c: DistanceX(g8,g-1) = 50
    c: Equal(g4,g5)
    c: Equal(g5,g6)
    c: Equal(g6,g7)
    c: Coincident(g9,g8)
    c: PointOnObject(g9,g0)
    c: Vertical(g9)
    c: Symmetric(g4,g5,g9)
    c: Symmetric(g7,g6,g9)
    c: Vertical(g6,g5)
    c: PointOnObject(g10,g3)
    c: Symmetric(g1,g0,g10)
    c: Diameter(g6) = 4.5
    c: DistanceX(g4,g5) = 80
    c: DistanceY(g7,g4) = 25
    c: DistanceX(g0,g0) = 70
    c: DistanceY(g1,g1) = 62
    c: DistanceY(g-1,g1) = 31
    c: Horizontal(g10)
    c: Coincident(g11,g6)
    c: Coincident(g11,g5)
    c: Symmetric(g6,g5,g12)
    c: DistanceY(g1,g12) = 29
FEATURE [PartDesign::Pocket] Pocket021
  BaseFeature = -> Pad016
  Direction = (0,0.707107,-0.707107)
  Length = 5
  Length2 = 100
  Profile = -> Sketch051
  Type = 0
FEATURE [PartDesign::Body] Body002  label="faceAvant"
  BaseFeature = -> Slice_child1
  Group = -> [Clone001,Thickness001,DatumPlane007,Sketch016,Pad005,Sketch017,Pad006,Sketch018,Pocket010,DatumPlane011,Sketch030,Pad014,Pad015,Sketch031,Pad016,Sketch051,Pocket021]
  Origin = -> Origin003
  Tip = -> Pocket021
COMPONENT P2 — recipe-attached ("visTHCM3x6_FAV001", modeled in this document).
Construction recipe (the document's own serialized feature program — sketch geometry with constraints, then the solid features built on it; lengths are millimeters unless a unit is written):

FEATURE [Sketcher::SketchObject] Sketch034  label="Sketch"
  FullyConstrained = false
  MapMode = 5
  Support = -> [XY_Plane015]
  sketch-geometry (1):
    g0: Circle CenterX=0 CenterY=0 CenterZ=0 NormalX=0 NormalY=0 NormalZ=1 AngleXU=0 Radius=2.75
  constraints (2):
    c: Coincident(g0,g-1)
    c: Diameter(g0) = 5.5
FEATURE [PartDesign::Pad] Pad019  label="tete"
  AllowMultiFace = false
  Direction = (1,1,1)
  Length = 3
  Length2 = 100
  Profile = -> Sketch034
  Type = 0
FEATURE [Sketcher::SketchObject] Sketch001
  FullyConstrained = false
  MapMode = 5
  Placement = pos=(0,0,0) rot=(1,0,0;3.14159rad)
  Support = -> [Pad019]
  sketch-geometry (1):
    g0: Circle CenterX=0 CenterY=0 CenterZ=0 NormalX=0 NormalY=0 NormalZ=1 AngleXU=0 Radius=1.5
  constraints (2):
    c: Coincident(g0,g-1)
    c: Diameter(g0) = 3
FEATURE [PartDesign::Pad] Pad020  label="corps"
  AllowMultiFace = false
  BaseFeature = -> Pad019
  Direction = (1,1,1)
  Length = 6
  Length2 = 100
  Profile = -> Sketch001
  Type = 0
FEATURE [PartDesign::Plane] DatumPlane014
  AttachmentOffset = pos=(0,0,3) rot=(0,0,1;0rad)
  Length = 60
  MapMode = 5
  Placement = pos=(0,0,3) rot=(0,0,1;0rad)
  ResizeMode = 0
  Support = -> [XY_Plane015]
  Width = 60
FEATURE [Sketcher::SketchObject] Sketch035  label="Sketch002"
  FullyConstrained = false
  MapMode = 5
  Placement = pos=(0,0,3) rot=(0,0,1;0rad)
  Support = -> [DatumPlane014]
  sketch-geometry (7):
    g0: LineSegment StartX=0.721688 StartY=-1.25 StartZ=0 EndX=1.44338 EndY=1.0119e-12 EndZ=0
    g1: LineSegment StartX=1.44338 StartY=1.0119e-12 StartZ=0 EndX=0.721688 EndY=1.25 EndZ=0
    g2: LineSegment StartX=0.721688 StartY=1.25 StartZ=0 EndX=-0.721688 EndY=1.25 EndZ=0
    g3: LineSegment StartX=-0.721688 StartY=1.25 StartZ=0 EndX=-1.44338 EndY=8.689e-13 EndZ=0
    g4: LineSegment StartX=-1.44338 StartY=8.689e-13 StartZ=0 EndX=-0.721688 EndY=-1.25 EndZ=0
    g5: LineSegment StartX=-0.721688 StartY=-1.25 StartZ=0 EndX=0.721688 EndY=-1.25 EndZ=0
    g6: Circle CenterX=0 CenterY=0 CenterZ=0 NormalX=0 NormalY=0 NormalZ=1 AngleXU=0 Radius=1.44338
  constraints (16):
    c: Coincident(g0,g1)
    c: Coincident(g1,g2)
    c: Coincident(g2,g3)
    c: Coincident(g3,g4)
    c: Coincident(g4,g5)
    c: Coincident(g5,g0)
    c: Equal(g0, g1-g5) x5
    c: PointOnObject(g0,g6)
    c: PointOnObject(g1,g6)
    c: PointOnObject(g2,g6)
    c: PointOnObject(g3,g6)
    c: PointOnObject(g4,g6)
    c: PointOnObject(g5,g6)
    c: Coincident(g6,g-1)
    c: Horizontal(g2)
    c: DistanceY(g0,g1) = 2.5
FEATURE [PartDesign::Pocket] Pocket016  label="emprunte"
  AllowMultiFace = false
  BaseFeature = -> Pad020
  Direction = (1,1,1)
  Length = 4
  Length2 = 100
  Profile = -> Sketch035
  Type = 0
FEATURE [PartDesign::Body] Body009  label="visTHCM3x6_FAV001"
  Group = -> [Sketch034,Pad019,Sketch001,Pad020,DatumPlane014,Sketch035,Pocket016]
  Origin = -> Origin019
  Placement = pos=(-6.5,-61.8718,6.01041) rot=(1,0,0;3.92699rad)
  Tip = -> Pocket016
COMPONENT P3 — recipe-attached ("visTHCM3x6_FAV002", modeled in this document).
Construction recipe (the document's own serialized feature program — sketch geometry with constraints, then the solid features built on it; lengths are millimeters unless a unit is written):

FEATURE [Sketcher::SketchObject] Sketch036
  FullyConstrained = false
  MapMode = 5
  Support = -> [XY_Plane016]
  sketch-geometry (1):
    g0: Circle CenterX=0 CenterY=0 CenterZ=0 NormalX=0 NormalY=0 NormalZ=1 AngleXU=0 Radius=2.75
  constraints (2):
    c: Coincident(g0,g-1)
    c: Diameter(g0) = 5.5
FEATURE [PartDesign::Pad] Pad021  label="tete001"
  AllowMultiFace = false
  Direction = (1,1,1)
  Length = 3
  Length2 = 100
  Profile = -> Sketch036
  Type = 0
FEATURE [Sketcher::SketchObject] Sketch037
  FullyConstrained = false
  MapMode = 5
  Placement = pos=(0,0,0) rot=(1,0,0;3.14159rad)
  Support = -> [Pad021]
  sketch-geometry (1):
    g0: Circle CenterX=0 CenterY=0 CenterZ=0 NormalX=0 NormalY=0 NormalZ=1 AngleXU=0 Radius=1.5
  constraints (2):
    c: Coincident(g0,g-1)
    c: Diameter(g0) = 3
FEATURE [PartDesign::Pad] Pad022  label="corps001"
  AllowMultiFace = false
  BaseFeature = -> Pad021
  Direction = (1,1,1)
  Length = 6
  Length2 = 100
  Profile = -> Sketch037
  Type = 0
FEATURE [PartDesign::Plane] DatumPlane015
  AttachmentOffset = pos=(0,0,3) rot=(0,0,1;0rad)
  Length = 60
  MapMode = 5
  Placement = pos=(0,0,3) rot=(0,0,1;0rad)
  ResizeMode = 0
  Support = -> [XY_Plane016]
  Width = 60
FEATURE [Sketcher::SketchObject] Sketch038
  FullyConstrained = false
  MapMode = 5
  Placement = pos=(0,0,3) rot=(0,0,1;0rad)
  Support = -> [DatumPlane015]
  sketch-geometry (7):
    g0: LineSegment StartX=0.721688 StartY=-1.25 StartZ=0 EndX=1.44338 EndY=1.0119e-12 EndZ=0
    g1: LineSegment StartX=1.44338 StartY=1.0119e-12 StartZ=0 EndX=0.721688 EndY=1.25 EndZ=0
    g2: LineSegment StartX=0.721688 StartY=1.25 StartZ=0 EndX=-0.721688 EndY=1.25 EndZ=0
    g3: LineSegment StartX=-0.721688 StartY=1.25 StartZ=0 EndX=-1.44338 EndY=8.689e-13 EndZ=0
    g4: LineSegment StartX=-1.44338 StartY=8.689e-13 StartZ=0 EndX=-0.721688 EndY=-1.25 EndZ=0
    g5: LineSegment StartX=-0.721688 StartY=-1.25 StartZ=0 EndX=0.721688 EndY=-1.25 EndZ=0
    g6: Circle CenterX=0 CenterY=0 CenterZ=0 NormalX=0 NormalY=0 NormalZ=1 AngleXU=0 Radius=1.44338
  constraints (16):
    c: Coincident(g0,g1)
    c: Coincident(g1,g2)
    c: Coincident(g2,g3)
    c: Coincident(g3,g4)
    c: Coincident(g4,g5)
    c: Coincident(g5,g0)
    c: Equal(g0, g1-g5) x5
    c: PointOnObject(g0,g6)
    c: PointOnObject(g1,g6)
    c: PointOnObject(g2,g6)
    c: PointOnObject(g3,g6)
    c: PointOnObject(g4,g6)
    c: PointOnObject(g5,g6)
    c: Coincident(g6,g-1)
    c: Horizontal(g2)
    c: DistanceY(g0,g1) = 2.5
FEATURE [PartDesign::Pocket] Pocket017  label="emprunte001"
  AllowMultiFace = false
  BaseFeature = -> Pad022
  Direction = (1,1,1)
  Length = 4
  Length2 = 100
  Profile = -> Sketch038
  Type = 0
FEATURE [PartDesign::Body] Body010  label="visTHCM3x6_FAV002"
  Group = -> [Sketch036,Pad021,Sketch037,Pad022,DatumPlane015,Sketch038,Pocket017]
  Origin = -> Origin020
  Placement = pos=(-118.5,-61.8718,6.01041) rot=(1,0,0;3.92699rad)
  Tip = -> Pocket017
COMPONENT P4 — recipe-attached ("dgispark", modeled in this document).
Construction recipe (the document's own serialized feature program — sketch geometry with constraints, then the solid features built on it; lengths are millimeters unless a unit is written):

FEATURE [Sketcher::SketchObject] Sketch  label="profileDeBase"
  FullyConstrained = true
  MapMode = 5
  Placement = pos=(0,0,0) rot=(0.57735,0.57735,0.57735;2.0944rad)
  Support = -> [YZ_Plane001]
  expr: Constraints[10] = <<sp>>.petitRetour
  expr: Constraints[11] = <<sp>>.angleFacePetitRetour
  expr: Constraints[12] = <<sp>>.Face
  expr: Constraints[13] = <<sp>>.angleFaceRetourHaut
  expr: Constraints[8] = <<sp>>.Base
  expr: Constraints[9] = <<sp>>.anglePetitRetourBase
  sketch-geometry (5):
    g0: LineSegment StartX=0 StartY=0 StartZ=0 EndX=-65 EndY=0 EndZ=0
    g1: LineSegment StartX=-65 StartY=0 StartZ=0 EndX=-79.1421 EndY=14.1421 EndZ=0
    g2: LineSegment StartX=-79.1421 StartY=14.1421 StartZ=0 EndX=-22.5736 EndY=70.7107 EndZ=0
    g3: LineSegment StartX=-22.5736 StartY=70.7107 StartZ=0 EndX=0 EndY=48.1371 EndZ=0
    g4: LineSegment StartX=0 StartY=48.1371 StartZ=0 EndX=0 EndY=0 EndZ=0
  constraints (14):
    c: Coincident(g-1,g0)
    c: Horizontal(g0)
    c: Coincident(g0,g1)
    c: Coincident(g1,g2)
    c: Coincident(g2,g3)
    c: PointOnObject(g3,g-2)
    c: Coincident(g3,g4)
    c: Coincident(g4,g0)
    c: DistanceX(g0,g0) = 65
    c: Angle(g0,g1) = 2.35619
    c: Distance(g1) = 20
    c: Angle(g1,g2) = 1.5708
    c: Distance(g2) = 80
    c: Angle(g2,g3) = 1.5708
FEATURE [PartDesign::Pad] Pad
  AllowMultiFace = false
  Direction = (1,1,1)
  Length = 100
  Length2 = 100
  Placement = pos=(0,0,0) rot=(0.57735,0.57735,0.57735;2.0944rad)
  Profile = -> Sketch
  Reversed = true
  Type = 0
  expr: Length = <<sp>>.largeurModuleBase
FEATURE [PartDesign::Plane] DatumPlane
  AttachmentOffset = pos=(71,0,0) rot=(0,-1,0;0.785398rad)
  Length = 98.6412
  MapMode = 5
  Placement = pos=(-7.9e-15,8e-15,71) rot=(0.678598,0.678598,0.281085;3.68962rad)
  ResizeMode = 0
  Support = -> [Pad]
  Width = 63.0813
FEATURE [PartDesign::Body] Body  label="Base"
  Group = -> [Sketch,Pad,DatumPlane]
  Origin = -> Origin001
  Tip = -> Pad
COMPONENT P5 — geometry summary ("fanSupportPartLnk"; no construction recipe available for this part):
  bounding box: 136.9 x 112.3 x 92.4 mm
  tessellated surface: 166,740 triangles
  volume: 194544 mm^3 (14% of its bounding box)
COMPONENT P6 — geometry summary ("xt60fem"; no construction recipe available for this part):
  bounding box: 20.5 x 16.5 x 7.5 mm
  tessellated surface: 16,084 triangles
  volume: 955 mm^3 (38% of its bounding box)
COMPONENT P7 — geometry summary ("xt60Male"; no construction recipe available for this part):
  bounding box: 20.2 x 16.6 x 7.5 mm
  tessellated surface: 12,256 triangles
  volume: 1201 mm^3 (48% of its bounding box)
COMPONENT P8 — geometry summary ("ZSB_RUTHEX_M3_5.7_002"; no construction recipe available for this part):
  bounding box: 5.7 x 4.6 x 4.6 mm
  tessellated surface: 4,392 triangles
  volume: 44 mm^3 (36% of its bounding box)
  symmetry: 4-fold rotationally symmetric about the y axis; mirror-symmetric across its x mid-plane, z mid-plane
COMPONENT P9 — geometry summary ("ZSB_RUTHEX_M3_5.7_003"; no construction recipe available for this part):
  bounding box: 6.9 x 6.9 x 4.6 mm
  tessellated surface: 4,392 triangles
  volume: 44 mm^3 (20% of its bounding box)
  symmetry: mirror-symmetric across its x mid-plane
COMPONENT P10 — geometry summary ("ZSB_RUTHEX_M3_5.7_004"; no construction recipe available for this part):
  bounding box: 6.9 x 6.9 x 4.6 mm
  tessellated surface: 4,392 triangles
  volume: 44 mm^3 (20% of its bounding box)
  symmetry: mirror-symmetric across its x mid-plane
COMPONENT P11 — recipe-attached ("partVisPointeauM3x10_001", modeled in this document).
Construction recipe (the document's own serialized feature program — sketch geometry with constraints, then the solid features built on it; lengths are millimeters unless a unit is written):

FEATURE [Sketcher::SketchObject] Sketch025
  FullyConstrained = false
  MapMode = 5
  Support = -> [XY_Plane008]
  sketch-geometry (1):
    g0: Circle CenterX=0 CenterY=0 CenterZ=0 NormalX=0 NormalY=0 NormalZ=1 AngleXU=0 Radius=1.5
  constraints (2):
    c: Coincident(g0,g-1)
    c: Diameter(g0) = 3
FEATURE [Sketcher::SketchObject] Sketch026
  FullyConstrained = false
  MapMode = 5
  Support = -> [XY_Plane008]
  sketch-geometry (7):
    g0: LineSegment StartX=0.433013 StartY=-0.75 StartZ=0 EndX=0.866025 EndY=1.25568e-11 EndZ=0
    g1: LineSegment StartX=0.866025 StartY=1.25568e-11 StartZ=0 EndX=0.433013 EndY=0.75 EndZ=0
    g2: LineSegment StartX=0.433013 StartY=0.75 StartZ=0 EndX=-0.433013 EndY=0.75 EndZ=0
    g3: LineSegment StartX=-0.433013 StartY=0.75 StartZ=0 EndX=-0.866025 EndY=2.91366e-11 EndZ=0
    g4: LineSegment StartX=-0.866025 StartY=2.91366e-11 StartZ=0 EndX=-0.433013 EndY=-0.75 EndZ=0
    g5: LineSegment StartX=-0.433013 StartY=-0.75 StartZ=0 EndX=0.433013 EndY=-0.75 EndZ=0
    g6: Circle CenterX=0 CenterY=0 CenterZ=0 NormalX=0 NormalY=0 NormalZ=1 AngleXU=0 Radius=0.866025
  constraints (16):
    c: Coincident(g0,g1)
    c: Coincident(g1,g2)
    c: Coincident(g2,g3)
    c: Coincident(g3,g4)
    c: Coincident(g4,g5)
    c: Coincident(g5,g0)
    c: Equal(g0, g1-g5) x5
    c: PointOnObject(g0,g6)
    c: PointOnObject(g1,g6)
    c: PointOnObject(g2,g6)
    c: PointOnObject(g3,g6)
    c: PointOnObject(g4,g6)
    c: PointOnObject(g5,g6)
    c: Coincident(g6,g-1)
    c: Horizontal(g2)
    c: DistanceY(g0,g1) = 1.5
FEATURE [PartDesign::Pad] Pad012
  AllowMultiFace = false
  Direction = (1,1,1)
  Length = 10
  Length2 = 100
  Profile = -> Sketch025
  Type = 0
FEATURE [PartDesign::Chamfer] Chamfer
  Angle = 45
  Base = -> Pad012 [Edge3]
  BaseFeature = -> Pad012
  ChamferType = 0
  FlipDirection = false
  Size = 1.4
  Size2 = 1
  SupportTransform = false
  UseAllEdges = false
FEATURE [PartDesign::Pocket] Pocket013
  AllowMultiFace = false
  BaseFeature = -> Chamfer
  Direction = (1,1,1)
  Length = 1.5
  Length2 = 100
  Profile = -> Sketch026
  Reversed = true
  Type = 0
FEATURE [PartDesign::Chamfer] Chamfer001
  Angle = 45
  Base = -> Pocket013 [Edge3]
  BaseFeature = -> Pocket013
  ChamferType = 0
  FlipDirection = false
  Size = 0.1
  Size2 = 1
  SupportTransform = false
  UseAllEdges = false
FEATURE [PartDesign::Body] Body005  label="bodyVisPointeauM3x10_001"
  Group = -> [Sketch025,Pad012,Chamfer,Sketch026,Pocket013,Chamfer001]
  Origin = -> Origin013
  Tip = -> Chamfer001
COMPONENT P12 — recipe-attached ("partVisPointeauM3x10_002", modeled in this document).
Construction recipe (the document's own serialized feature program — sketch geometry with constraints, then the solid features built on it; lengths are millimeters unless a unit is written):

FEATURE [Sketcher::SketchObject] Sketch027
  FullyConstrained = false
  MapMode = 5
  Support = -> [XY_Plane010]
  sketch-geometry (7):
    g0: LineSegment StartX=0.433013 StartY=-0.75 StartZ=0 EndX=0.866025 EndY=1.25568e-11 EndZ=0
    g1: LineSegment StartX=0.866025 StartY=1.25568e-11 StartZ=0 EndX=0.433013 EndY=0.75 EndZ=0
    g2: LineSegment StartX=0.433013 StartY=0.75 StartZ=0 EndX=-0.433013 EndY=0.75 EndZ=0
    g3: LineSegment StartX=-0.433013 StartY=0.75 StartZ=0 EndX=-0.866025 EndY=2.91366e-11 EndZ=0
    g4: LineSegment StartX=-0.866025 StartY=2.91366e-11 StartZ=0 EndX=-0.433013 EndY=-0.75 EndZ=0
    g5: LineSegment StartX=-0.433013 StartY=-0.75 StartZ=0 EndX=0.433013 EndY=-0.75 EndZ=0
    g6: Circle CenterX=0 CenterY=0 CenterZ=0 NormalX=0 NormalY=0 NormalZ=1 AngleXU=0 Radius=0.866025
  constraints (16):
    c: Coincident(g0,g1)
    c: Coincident(g1,g2)
    c: Coincident(g2,g3)
    c: Coincident(g3,g4)
    c: Coincident(g4,g5)
    c: Coincident(g5,g0)
    c: Equal(g0, g1-g5) x5
    c: PointOnObject(g0,g6)
    c: PointOnObject(g1,g6)
    c: PointOnObject(g2,g6)
    c: PointOnObject(g3,g6)
    c: PointOnObject(g4,g6)
    c: PointOnObject(g5,g6)
    c: Coincident(g6,g-1)
    c: Horizontal(g2)
    c: DistanceY(g0,g1) = 1.5
FEATURE [Sketcher::SketchObject] Sketch028
  FullyConstrained = false
  MapMode = 5
  Support = -> [XY_Plane010]
  sketch-geometry (1):
    g0: Circle CenterX=0 CenterY=0 CenterZ=0 NormalX=0 NormalY=0 NormalZ=1 AngleXU=0 Radius=1.5
  constraints (2):
    c: Coincident(g0,g-1)
    c: Diameter(g0) = 3
FEATURE [PartDesign::Pad] Pad013
  AllowMultiFace = false
  Direction = (1,1,1)
  Length = 10
  Length2 = 100
  Profile = -> Sketch028
  Type = 0
FEATURE [PartDesign::Chamfer] Chamfer003
  Angle = 45
  Base = -> Pad013 [Edge3]
  BaseFeature = -> Pad013
  ChamferType = 0
  FlipDirection = false
  Size = 1.4
  Size2 = 1
  SupportTransform = false
  UseAllEdges = false
FEATURE [PartDesign::Pocket] Pocket014
  AllowMultiFace = false
  BaseFeature = -> Chamfer003
  Direction = (1,1,1)
  Length = 1.5
  Length2 = 100
  Profile = -> Sketch027
  Reversed = true
  Type = 0
FEATURE [PartDesign::Chamfer] Chamfer002
  Angle = 45
  Base = -> Pocket014 [Edge3]
  BaseFeature = -> Pocket014
  ChamferType = 0
  FlipDirection = false
  Size = 0.1
  Size2 = 1
  SupportTransform = false
  UseAllEdges = false
FEATURE [PartDesign::Body] Body006  label="bodyVisPointeauM3x10_002"
  Group = -> [Sketch028,Pad013,Chamfer003,Sketch027,Pocket014,Chamfer002]
  Origin = -> Origin015
  Tip = -> Chamfer002
COMPONENT P13 — recipe-attached ("tigeLaiton001", modeled in this document).
Construction recipe (the document's own serialized feature program — sketch geometry with constraints, then the solid features built on it; lengths are millimeters unless a unit is written):

FEATURE [PartDesign::Plane] DatumPlane012  label="planBaseTige"
  AttachmentOffset = pos=(0,0,-5.18) rot=(0,0,1;0rad)
  Length = 60
  MapMode = 5
  Placement = pos=(-5.18,1.2e-15,-1.2e-15) rot=(0.57735,0.57735,0.57735;2.0944rad)
  ResizeMode = 0
  Support = -> [YZ_Plane012]
  Width = 60
  expr: .AttachmentOffset.Base.z = -<<tige>>.planBaseTigeposX
FEATURE [Sketcher::SketchObject] Sketch032  label="sk_tiges"
  FullyConstrained = true
  MapMode = 5
  Placement = pos=(-5.18,1.2e-15,-1.2e-15) rot=(0.57735,0.57735,0.57735;2.0944rad)
  Support = -> [DatumPlane012]
  expr: Constraints[0] = <<tige>>.tigeDiam
  expr: Constraints[1] = <<tige>>.tigePosY
  expr: Constraints[2] = <<tige>>.tigePosX
  sketch-geometry (1):
    g0: Circle CenterX=-14 CenterY=14.3 CenterZ=0 NormalX=0 NormalY=0 NormalZ=1 AngleXU=0 Radius=1.25
  constraints (3):
    c: Diameter(g0) = 2.5
    c: DistanceY(g-1,g0) = 14.3
    c: DistanceX(g0,g-1) = 14
FEATURE [PartDesign::Pad] Pad017  label="tigeBasse"
  AllowMultiFace = false
  Direction = (1,1,1)
  Length = 83.62
  Length2 = 100
  Placement = pos=(-5.18,1e-15,-1e-15) rot=(0.57735,0.57735,0.57735;2.0944rad)
  Profile = -> Sketch032
  Reversed = true
  Type = 0
  expr: Length = <<tige>>.tigeLong
FEATURE [PartDesign::Body] Body007  label="tigeLaiton"
  Group = -> [DatumPlane012,Sketch032,Pad017]
  Origin = -> Origin016
  Tip = -> Pad017
FEATURE [PartDesign::Plane] DatumPlane013  label="planTige2"
  AttachmentOffset = pos=(0,0,-5.18) rot=(0,0,1;0rad)
  Length = 60
  MapMode = 5
  Placement = pos=(-5.18,1.2e-15,-1.2e-15) rot=(0.57735,0.57735,0.57735;2.0944rad)
  ResizeMode = 0
  Support = -> [YZ_Plane014]
  Width = 60
  expr: .AttachmentOffset.Base.z = -<<tige>>.planBaseTigeposX
FEATURE [Sketcher::SketchObject] Sketch033  label="sk_tige2"
  FullyConstrained = true
  MapMode = 5
  Placement = pos=(-5.18,1.2e-15,-1.2e-15) rot=(0.57735,0.57735,0.57735;2.0944rad)
  Support = -> [DatumPlane013]
  expr: Constraints[0] = <<tige>>.tigeDiam
  expr: Constraints[1] = <<tige>>.tigePosX
  expr: Constraints[2] = <<tige>>.tigePosY + <<tige>>.xtEcartBroches
  sketch-geometry (1):
    g0: Circle CenterX=-14 CenterY=21.86 CenterZ=0 NormalX=0 NormalY=0 NormalZ=1 AngleXU=0 Radius=1.25
  constraints (3):
    c: Diameter(g0) = 2.5
    c: DistanceX(g0,g-1) = 14
    c: DistanceY(g-1,g0) = 21.86
FEATURE [PartDesign::Pad] Pad018
  AllowMultiFace = false
  Direction = (1,1,1)
  Length = 83.62
  Length2 = 100
  Placement = pos=(-5.18,1e-15,-1e-15) rot=(0.57735,0.57735,0.57735;2.0944rad)
  Profile = -> Sketch033
  Reversed = true
  Type = 0
  expr: Length = <<tige>>.tigeLong
FEATURE [PartDesign::Body] Body008  label="tige2"
  Group = -> [DatumPlane013,Sketch033,Pad018]
  Origin = -> Origin018
  Tip = -> Pad018
COMPONENT P14 — recipe-attached ("DCDCVisInsert", modeled in this document).
Construction recipe (the document's own serialized feature program — sketch geometry with constraints, then the solid features built on it; lengths are millimeters unless a unit is written):

FEATURE [Sketcher::SketchObject] Sketch045
  FullyConstrained = false
  MapMode = 5
  Support = -> [XY_Plane024]
  sketch-geometry (1):
    g0: Circle CenterX=0 CenterY=0 CenterZ=0 NormalX=0 NormalY=0 NormalZ=1 AngleXU=0 Radius=2.75
  constraints (2):
    c: Coincident(g0,g-1)
    c: Diameter(g0) = 5.5
FEATURE [PartDesign::Pad] Pad023  label="tete002"
  AllowMultiFace = false
  Direction = (1,1,1)
  Length = 3
  Length2 = 100
  Profile = -> Sketch045
  Type = 0
FEATURE [Sketcher::SketchObject] Sketch046
  FullyConstrained = false
  MapMode = 5
  Placement = pos=(0,0,0) rot=(1,0,0;3.14159rad)
  Support = -> [Pad023]
  sketch-geometry (1):
    g0: Circle CenterX=0 CenterY=0 CenterZ=0 NormalX=0 NormalY=0 NormalZ=1 AngleXU=0 Radius=1.5
  constraints (2):
    c: Coincident(g0,g-1)
    c: Diameter(g0) = 3
FEATURE [PartDesign::Pad] Pad024  label="corps002"
  AllowMultiFace = false
  BaseFeature = -> Pad023
  Direction = (1,1,1)
  Length = 6
  Length2 = 100
  Profile = -> Sketch046
  Type = 0
FEATURE [PartDesign::Plane] DatumPlane017  label="DatumPlane001"
  AttachmentOffset = pos=(0,0,3) rot=(0,0,1;0rad)
  Length = 60
  MapMode = 5
  Placement = pos=(0,0,3) rot=(0,0,1;0rad)
  ResizeMode = 0
  Support = -> [XY_Plane024]
  Width = 60
FEATURE [Sketcher::SketchObject] Sketch047  label="Sketch003"
  FullyConstrained = false
  MapMode = 5
  Placement = pos=(0,0,3) rot=(0,0,1;0rad)
  Support = -> [DatumPlane017]
  sketch-geometry (7):
    g0: LineSegment StartX=0.721688 StartY=-1.25 StartZ=0 EndX=1.44338 EndY=1.0119e-12 EndZ=0
    g1: LineSegment StartX=1.44338 StartY=1.0119e-12 StartZ=0 EndX=0.721688 EndY=1.25 EndZ=0
    g2: LineSegment StartX=0.721688 StartY=1.25 StartZ=0 EndX=-0.721688 EndY=1.25 EndZ=0
    g3: LineSegment StartX=-0.721688 StartY=1.25 StartZ=0 EndX=-1.44338 EndY=8.689e-13 EndZ=0
    g4: LineSegment StartX=-1.44338 StartY=8.689e-13 StartZ=0 EndX=-0.721688 EndY=-1.25 EndZ=0
    g5: LineSegment StartX=-0.721688 StartY=-1.25 StartZ=0 EndX=0.721688 EndY=-1.25 EndZ=0
    g6: Circle CenterX=0 CenterY=0 CenterZ=0 NormalX=0 NormalY=0 NormalZ=1 AngleXU=0 Radius=1.44338
  constraints (16):
    c: Coincident(g0,g1)
    c: Coincident(g1,g2)
    c: Coincident(g2,g3)
    c: Coincident(g3,g4)
    c: Coincident(g4,g5)
    c: Coincident(g5,g0)
    c: Equal(g0, g1-g5) x5
    c: PointOnObject(g0,g6)
    c: PointOnObject(g1,g6)
    c: PointOnObject(g2,g6)
    c: PointOnObject(g3,g6)
    c: PointOnObject(g4,g6)
    c: PointOnObject(g5,g6)
    c: Coincident(g6,g-1)
    c: Horizontal(g2)
    c: DistanceY(g0,g1) = 2.5
FEATURE [PartDesign::Pocket] Pocket019  label="emprunte002"
  AllowMultiFace = false
  BaseFeature = -> Pad024
  Direction = (1,1,1)
  Length = 4
  Length2 = 100
  Profile = -> Sketch047
  Type = 0
FEATURE [PartDesign::Body] Body014  label="visTHCM3x6_001"
  Group = -> [Sketch045,Pad023,Sketch046,Pad024,DatumPlane017,Sketch047,Pocket019]
  Origin = -> Origin028
  Placement = pos=(6.5,1.35,-19.25) rot=(-1,0,0;1.5708rad)
  Tip = -> Pocket019
FEATURE [Sketcher::SketchObject] Sketch049  label="Sketch005"
  FullyConstrained = false
  MapMode = 5
  Support = -> [XY_Plane025]
  sketch-geometry (1):
    g0: Circle CenterX=0 CenterY=0 CenterZ=0 NormalX=0 NormalY=0 NormalZ=1 AngleXU=0 Radius=2.75
  constraints (2):
    c: Coincident(g0,g-1)
    c: Diameter(g0) = 5.5
FEATURE [PartDesign::Pad] Pad025  label="tete003"
  AllowMultiFace = false
  Direction = (1,1,1)
  Length = 3
  Length2 = 100
  Profile = -> Sketch049
  Type = 0
FEATURE [Sketcher::SketchObject] Sketch050  label="Sketch006"
  FullyConstrained = false
  MapMode = 5
  Placement = pos=(0,0,0) rot=(1,0,0;3.14159rad)
  Support = -> [Pad025]
  sketch-geometry (1):
    g0: Circle CenterX=0 CenterY=0 CenterZ=0 NormalX=0 NormalY=0 NormalZ=1 AngleXU=0 Radius=1.5
  constraints (2):
    c: Coincident(g0,g-1)
    c: Diameter(g0) = 3
FEATURE [PartDesign::Pad] Pad002  label="corps003"
  AllowMultiFace = false
  BaseFeature = -> Pad025
  Direction = (1,1,1)
  Length = 6
  Length2 = 100
  Profile = -> Sketch050
  Type = 0
FEATURE [PartDesign::Plane] DatumPlane018  label="DatumPlane002"
  AttachmentOffset = pos=(0,0,3) rot=(0,0,1;0rad)
  Length = 60
  MapMode = 5
  Placement = pos=(0,0,3) rot=(0,0,1;0rad)
  ResizeMode = 0
  Support = -> [XY_Plane025]
  Width = 60
FEATURE [Sketcher::SketchObject] Sketch048  label="Sketch004"
  FullyConstrained = false
  MapMode = 5
  Placement = pos=(0,0,3) rot=(0,0,1;0rad)
  Support = -> [DatumPlane018]
  sketch-geometry (7):
    g0: LineSegment StartX=0.721688 StartY=-1.25 StartZ=0 EndX=1.44338 EndY=1.0119e-12 EndZ=0
    g1: LineSegment StartX=1.44338 StartY=1.0119e-12 StartZ=0 EndX=0.721688 EndY=1.25 EndZ=0
    g2: LineSegment StartX=0.721688 StartY=1.25 StartZ=0 EndX=-0.721688 EndY=1.25 EndZ=0
    g3: LineSegment StartX=-0.721688 StartY=1.25 StartZ=0 EndX=-1.44338 EndY=8.689e-13 EndZ=0
    g4: LineSegment StartX=-1.44338 StartY=8.689e-13 StartZ=0 EndX=-0.721688 EndY=-1.25 EndZ=0
    g5: LineSegment StartX=-0.721688 StartY=-1.25 StartZ=0 EndX=0.721688 EndY=-1.25 EndZ=0
    g6: Circle CenterX=0 CenterY=0 CenterZ=0 NormalX=0 NormalY=0 NormalZ=1 AngleXU=0 Radius=1.44338
  constraints (16):
    c: Coincident(g0,g1)
    c: Coincident(g1,g2)
    c: Coincident(g2,g3)
    c: Coincident(g3,g4)
    c: Coincident(g4,g5)
    c: Coincident(g5,g0)
    c: Equal(g0, g1-g5) x5
    c: PointOnObject(g0,g6)
    c: PointOnObject(g1,g6)
    c: PointOnObject(g2,g6)
    c: PointOnObject(g3,g6)
    c: PointOnObject(g4,g6)
    c: PointOnObject(g5,g6)
    c: Coincident(g6,g-1)
    c: Horizontal(g2)
    c: DistanceY(g0,g1) = 2.5
FEATURE [PartDesign::Pocket] Pocket020  label="emprunte003"
  AllowMultiFace = false
  BaseFeature = -> Pad002
  Direction = (1,1,1)
  Length = 4
  Length2 = 100
  Profile = -> Sketch048
  Type = 0
FEATURE [PartDesign::Body] Body015  label="visTHCM3x6_002"
  Group = -> [Sketch049,Pad025,Sketch050,Pad002,DatumPlane018,Sketch048,Pocket020]
  Origin = -> Origin029
  Placement = pos=(37.45,1.3,-2.5) rot=(-1,0,0;1.5708rad)
  Tip = -> Pocket020
PROVENANCE & LICENSES
A FreeCAD (.FCStd) document from a public repository crawl; recipes are the document's own serialized feature recipes (and, for linked parts, companion documents' recipes).
License: as declared in the source repository (recorded in the dataset sidecar).
